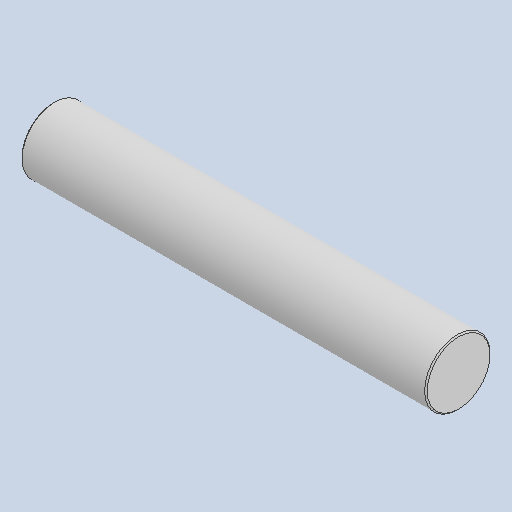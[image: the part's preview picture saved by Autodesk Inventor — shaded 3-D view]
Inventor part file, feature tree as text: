
AUTODESK INVENTOR PART (.ipt)
format: ipt  version: 2022 (Build 260153000, 153)  size: 82,432 bytes
history: native  units: in
note: dims shown in document units (in); Inventor stores cm internally (conversion verified against a paired STEP export)
features: chamfer x1
ambient origin geometry x8: Origin, YZ Plane, XZ Plane, XY Plane, X Axis, Y Axis, Z Axis, Center Point
bodies: Solid1 (feature_tree)
feature tree (1):
  chamfer  "Chamfer1"  [1 undecoded]
note: 1 required parameter value undecoded (feature->parameter linkage not recoverable at this tier; creation-order binding heuristic only, values carry confidence <= 0.55)
